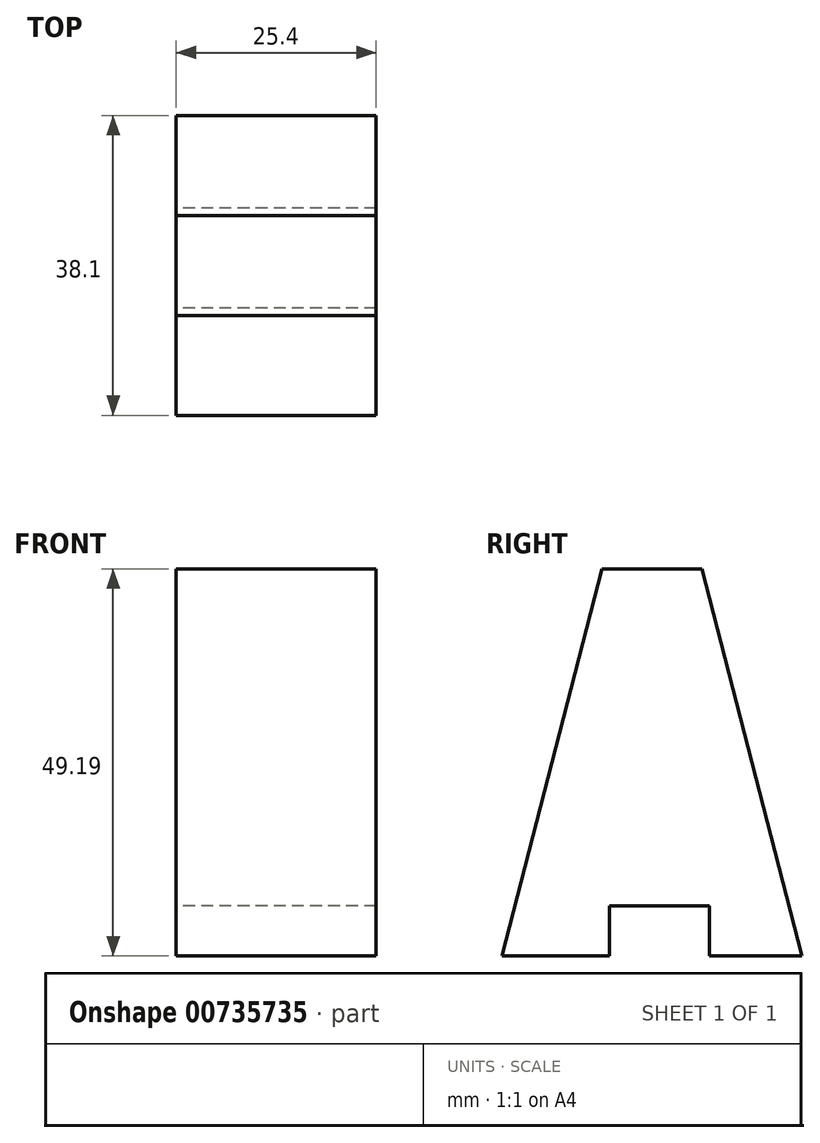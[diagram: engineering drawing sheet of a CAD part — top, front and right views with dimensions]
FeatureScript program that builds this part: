
annotation { "Feature Type Name" : "Feature", "Feature Type Description" : "" }
export const myFeature = defineFeature(function(context is Context, id is Id, definition is map)
    precondition{}
    {
        {
            var Q0;
            Q0=qCreatedBy(makeId("Right.planeOp"),FACE);
            var sketch = newSketch(context, id + "F0", { "sketchPlane" : qUnion([Q0])});
            skLineSegment(sketch, "E0", {"start": v(0, 0) * mm, "end": v(-12.7, 49.19) * mm});
            skLineSegment(sketch, "E1", {"start": v(-12.7, 49.19) * mm, "end": v(-25.4, 49.19) * mm});
            skLineSegment(sketch, "E2", {"start": v(-25.4, 49.19) * mm, "end": v(-38.1, 0) * mm});
            skLineSegment(sketch, "E3", {"start": v(-38.1, 0) * mm, "end": v(0, 0) * mm});
            skSolve(sketch);
        }
        {
            var Q0;
            Q0=makeQuery(id+"F0.imprint","IMPRINT",FACE,{"disambiguationData":[TD([[makeQuery(id+"F0.imprint","IMPRINT",EDGE,{"derivedFrom":sQuery(id+"F0.wireOp",EDGE,"E0")}),1.0]])]});
            extrude(context, id + "F1", {"entities" : qUnion([Q0]), "depth" : 25.4 * mm, "offsetDistance" : 25.4 * mm});
        }
        {
            var Q0;
            Q0=makeQuery(id+"F1.opExtrude","CAP_FACE",FACE,{"disambiguationData":[OSD([sQuery(id+"F0.wireOp",EDGE,"E0"),sQuery(id+"F0.wireOp",EDGE,"E1"),sQuery(id+"F0.wireOp",EDGE,"E2"),sQuery(id+"F0.wireOp",EDGE,"E3")])],"isStart":true});
            var sketch = newSketch(context, id + "F2", { "sketchPlane" : qUnion([Q0])});
            skLineSegment(sketch, "E4", {"start": v(11.76, 0) * mm, "end": v(11.76, 6.35) * mm});
            skLineSegment(sketch, "E5", {"start": v(11.76, 6.35) * mm, "end": v(24.46, 6.35) * mm});
            skLineSegment(sketch, "E6", {"start": v(24.46, 6.35) * mm, "end": v(24.46, 0) * mm});
            skLineSegment(sketch, "E7", {"start": v(24.46, 0) * mm, "end": v(11.76, 0) * mm});
            skSolve(sketch);
        }
        {
            var Q0;
            Q0=makeQuery(id+"F2.imprint","IMPRINT",FACE,{"disambiguationData":[TD([[makeQuery(id+"F2.imprint","IMPRINT",EDGE,{"derivedFrom":sQuery(id+"F2.wireOp",EDGE,"E4")}),-1.0]])]});
            extrude(context, id + "F3", {"entities" : qUnion([Q0]), "operationType" : NewBodyOperationType.REMOVE, "oppositeDirection" : true, "depth" : 25.4 * mm, "offsetDistance" : 25.4 * mm});
        }
    });
